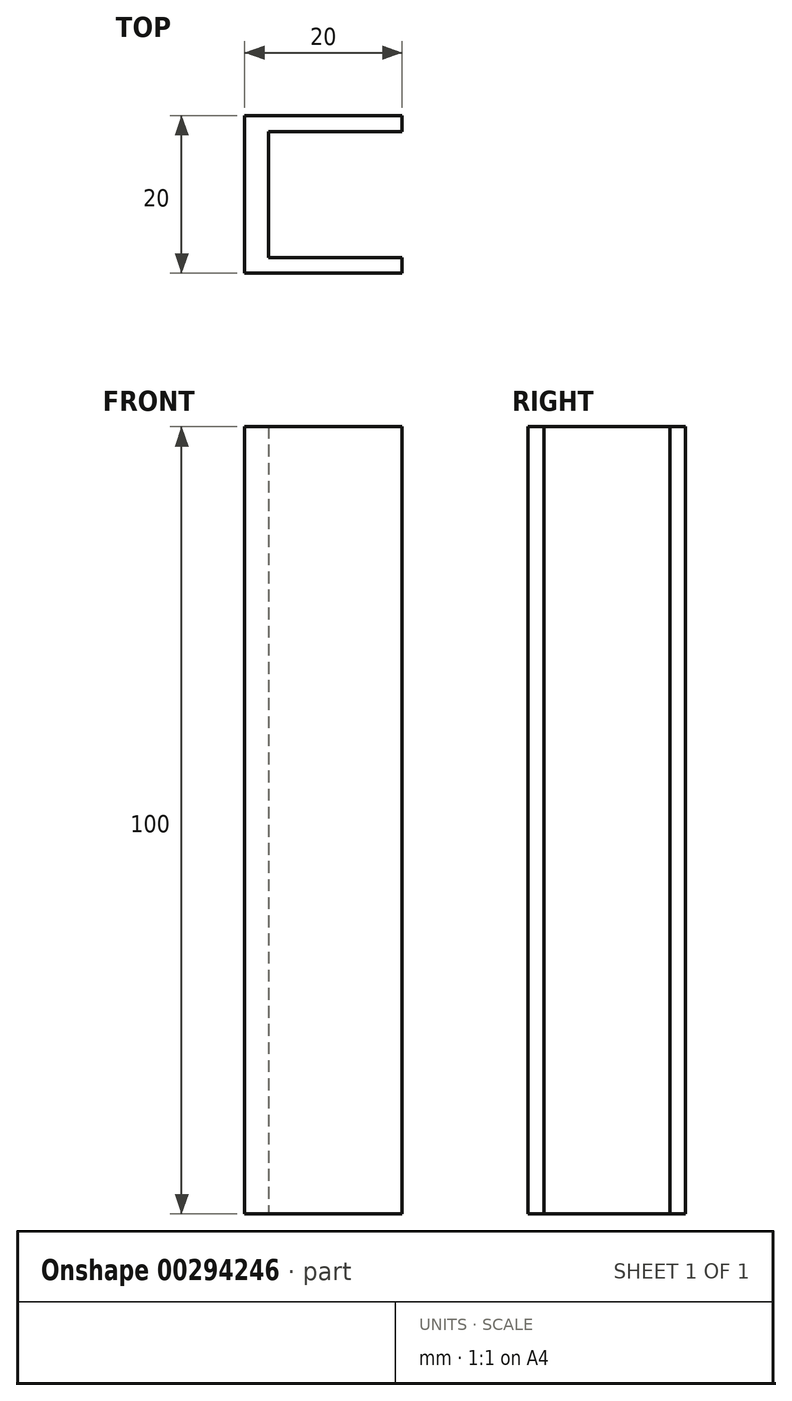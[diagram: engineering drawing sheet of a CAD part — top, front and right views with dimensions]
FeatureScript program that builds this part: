
annotation { "Feature Type Name" : "Feature", "Feature Type Description" : "" }
export const myFeature = defineFeature(function(context is Context, id is Id, definition is map)
    precondition{}
    {
        {
            var Q0;
            Q0=qCreatedBy(makeId("Top.planeOp"),FACE);
            var sketch = newSketch(context, id + "F0", { "sketchPlane" : qUnion([Q0])});
            skLineSegment(sketch, "E0.bottom", {"start": v(0, 0) * mm, "end": v(-20, 0) * mm});
            skLineSegment(sketch, "E0.top", {"start": v(0, 20) * mm, "end": v(-20, 20) * mm});
            skLineSegment(sketch, "E0.left", {"start": v(0, 0) * mm, "end": v(0, 2) * mm});
            skLineSegment(sketch, "E0.right", {"start": v(-20, 0) * mm, "end": v(-20, 20) * mm});
            skLineSegment(sketch, "E1.bottom", {"start": v(0, 18) * mm, "end": v(-17, 18) * mm});
            skLineSegment(sketch, "E1.top", {"start": v(0, 2) * mm, "end": v(-17, 2) * mm});
            skLineSegment(sketch, "E1.right", {"start": v(-17, 18) * mm, "end": v(-17, 2) * mm});
            skLineSegment(sketch, "E2.trimOffspring", {"start": v(0, 18) * mm, "end": v(0, 20) * mm});
            skSolve(sketch);
        }
        {
            var Q0;
            Q0 = qSketchRegion(id + "F0", true);
            extrude(context, id + "F1", {"entities" : qUnion([Q0]), "depth" : 100 * mm});
        }
    });
